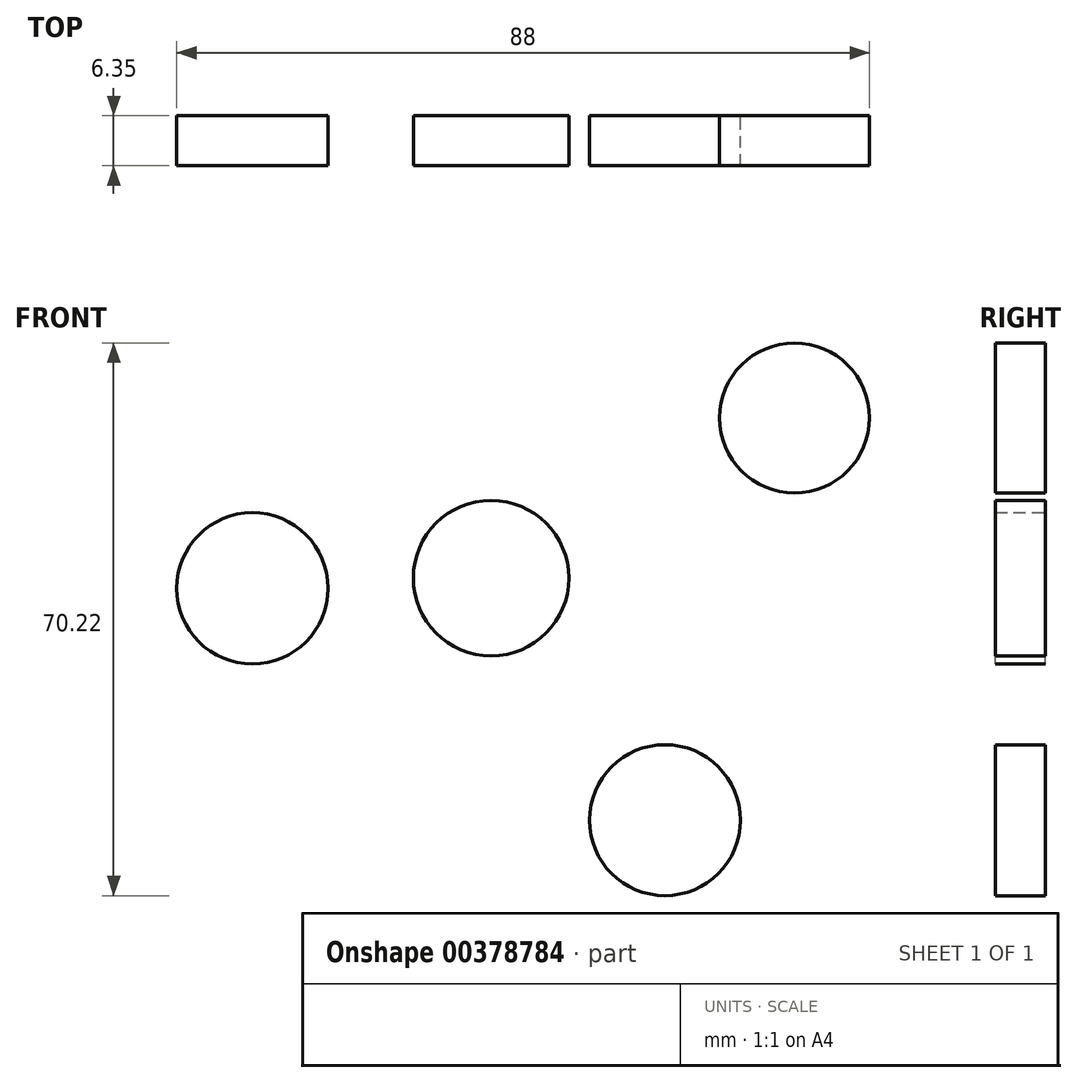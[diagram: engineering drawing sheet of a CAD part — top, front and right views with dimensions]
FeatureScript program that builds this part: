
annotation { "Feature Type Name" : "Feature", "Feature Type Description" : "" }
export const myFeature = defineFeature(function(context is Context, id is Id, definition is map)
    precondition{}
    {
        {
            var Q0;
            Q0=qCreatedBy(makeId("Front.planeOp"),FACE);
            var sketch = newSketch(context, id + "F0", { "sketchPlane" : qUnion([Q0])});
            skCircle(sketch, "E0", {"center": v(38.54, 51.1) * mm, "radius": 9.53 * mm});
            skCircle(sketch, "E1", {"center": v(22.09, 0) * mm, "radius": 9.59 * mm});
            skCircle(sketch, "E2", {"center": v(-30.31, 29.45) * mm, "radius": 9.62 * mm});
            skCircle(sketch, "E3", {"center": v(0, 30.75) * mm, "radius": 9.88 * mm});
            skSolve(sketch);
        }
        {
            var Q0;
            Q0 = qSketchRegion(id + "F0", true);
            extrude(context, id + "F1", {"entities" : qUnion([Q0]), "depth" : 6.35 * mm});
        }
    });
